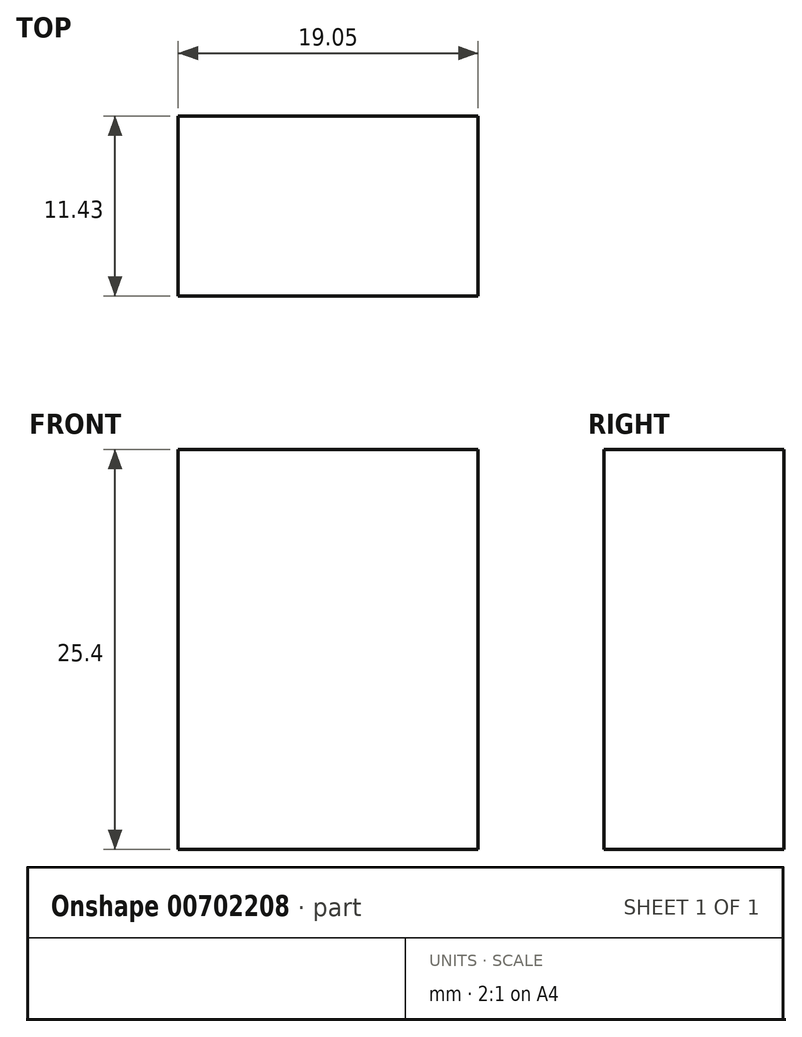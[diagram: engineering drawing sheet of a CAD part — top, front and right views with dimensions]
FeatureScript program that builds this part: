
annotation { "Feature Type Name" : "Feature", "Feature Type Description" : "" }
export const myFeature = defineFeature(function(context is Context, id is Id, definition is map)
    precondition{}
    {
        {
            var Q0;
            Q0=qCreatedBy(makeId("Front.planeOp"),FACE);
            var sketch = newSketch(context, id + "F0", { "sketchPlane" : qUnion([Q0])});
            skLineSegment(sketch, "E0.bottom", {"start": v(0, 0) * mm, "end": v(19.05, 0) * mm});
            skLineSegment(sketch, "E0.top", {"start": v(0, 25.4) * mm, "end": v(19.05, 25.4) * mm});
            skLineSegment(sketch, "E0.left", {"start": v(0, 0) * mm, "end": v(0, 25.4) * mm});
            skLineSegment(sketch, "E0.right", {"start": v(19.05, 0) * mm, "end": v(19.05, 25.4) * mm});
            skSolve(sketch);
        }
        {
            var Q0;
            Q0=makeQuery(id+"F0.imprint","IMPRINT",FACE,{"disambiguationData":[TD([[makeQuery(id+"F0.imprint","IMPRINT",EDGE,{"derivedFrom":sQuery(id+"F0.wireOp",EDGE,"E0.bottom")}),1.0]])]});
            extrude(context, id + "F1", {"entities" : qUnion([Q0]), "depth" : 11.43 * mm, "offsetDistance" : 25.4 * mm});
        }
    });
